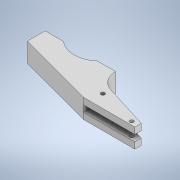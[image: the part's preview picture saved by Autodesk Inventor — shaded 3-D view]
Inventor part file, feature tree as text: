
AUTODESK INVENTOR PART (.ipt)
format: ipt  version: 2022 (Build 260153000, 153)  size: 127,488 bytes
history: native  units: mm
features: extrude x3, sketch x3
ambient origin geometry x8: Origin, YZ Plane, XZ Plane, XY Plane, X Axis, Y Axis, Z Axis, Center Point
bodies: Solid1 (feature_tree)
feature tree (6):
  extrude  "Extrusion1"  Depth=15.0mm
  extrude  "Extrusion2"  Depth=15.0mm TaperAngle=0.0deg
  extrude  "Extrusion3"  Depth=40.0mm
  sketch  "Sketch1"  dims[d11=15.0mm d12=0.0mm d14=3.0mm]
  sketch  "Sketch2"  dims[d17=3.0mm d18=15.0mm d19=0.0mm]
  sketch  "Sketch3"  dims[d20=5.0mm d21=40.0mm d22=5.0mm d23=44.75mm d24=0.0mm]
